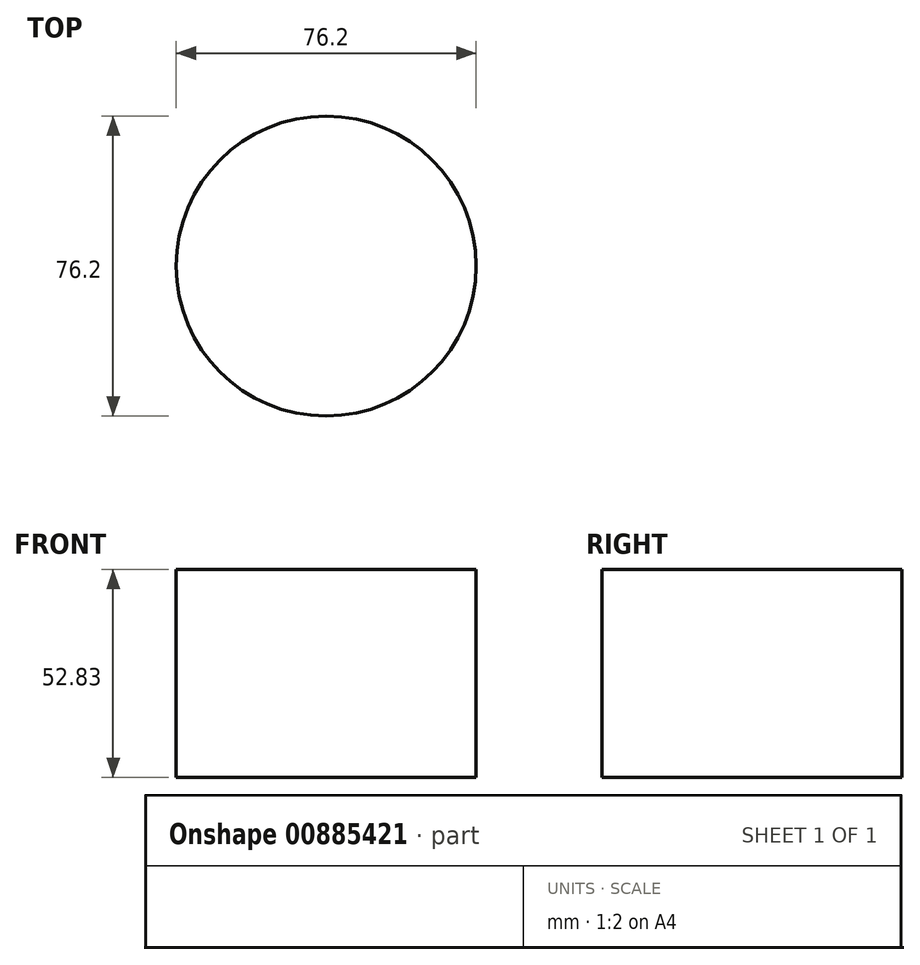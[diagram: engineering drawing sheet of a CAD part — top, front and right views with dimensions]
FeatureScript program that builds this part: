
annotation { "Feature Type Name" : "Feature", "Feature Type Description" : "" }
export const myFeature = defineFeature(function(context is Context, id is Id, definition is map)
    precondition{}
    {
        {
            var Q0;
            Q0=qCreatedBy(makeId("Top.planeOp"),FACE);
            var sketch = newSketch(context, id + "F0", { "sketchPlane" : qUnion([Q0])});
            skCircle(sketch, "E0", {"center": v(-116.2, -19.72) * mm, "radius": 38.1 * mm});
            skSolve(sketch);
        }
        {
            var Q0;
            Q0 = qSketchRegion(id + "F0", true);
            extrude(context, id + "F1", {"entities" : qUnion([Q0]), "depth" : 52.83 * mm, "offsetDistance" : 25.4 * mm});
        }
    });
